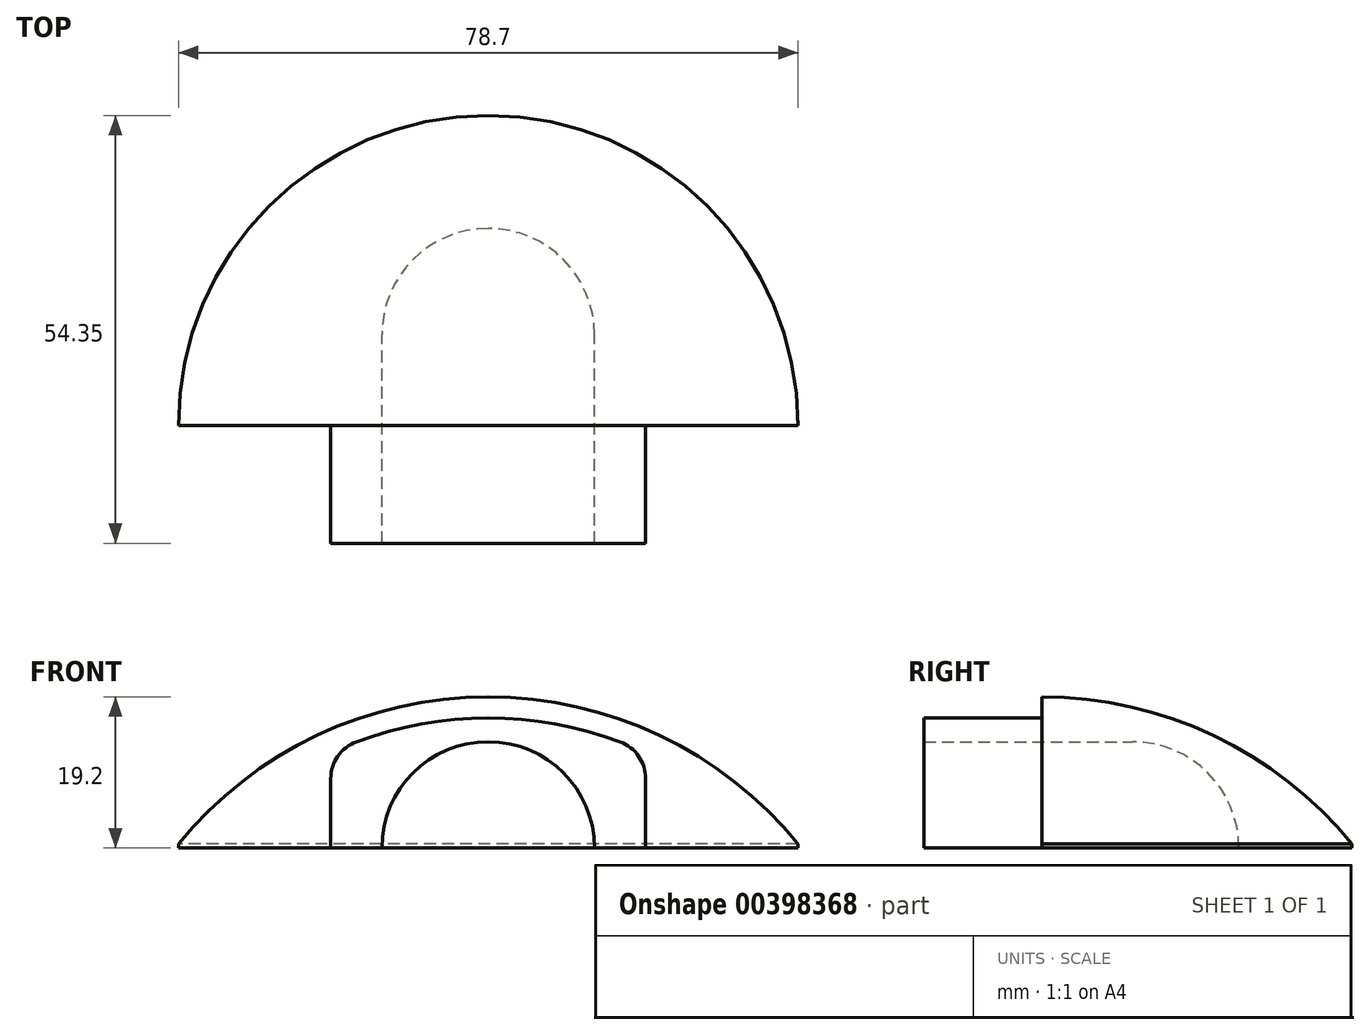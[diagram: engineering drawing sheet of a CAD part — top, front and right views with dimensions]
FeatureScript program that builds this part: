
annotation { "Feature Type Name" : "Feature", "Feature Type Description" : "" }
export const myFeature = defineFeature(function(context is Context, id is Id, definition is map)
    precondition{}
    {
        {
            var Q0;
            Q0=qCreatedBy(makeId("Front.planeOp"),FACE);
            var sketch = newSketch(context, id + "F0", { "sketchPlane" : qUnion([Q0])});
            skLineSegment(sketch, "E0", {"start": v(-39.5, 0) * mm, "end": v(39.5, 0) * mm});
            skPoint(sketch, "E1", {"position": v(0, 19) * mm});
            skLineSegment(sketch, "E2", {"start": v(39.5, 0) * mm, "end": v(39.5, 0) * mm});
            skLineSegment(sketch, "E3.MirrorCS", {"start": v(-39.5, 0) * mm, "end": v(-39.5, 0) * mm});
            skArc(sketch, "E4", {"start": v(39.5, 0) * mm, "mid": v(0, 19) * mm, "end": v(-39.5, 0) * mm});
            skSolve(sketch);
        }
        {
            var Q0;
            Q0=qCreatedBy(makeId("Front.planeOp"),FACE);
            var sketch = newSketch(context, id + "F1", { "sketchPlane" : qUnion([Q0])});
            skLineSegment(sketch, "E5.0", {"start": v(-39.35, 0) * mm, "end": v(0, 0) * mm});
            skArc(sketch, "E6.0", {"start": v(0, 19.2) * mm, "mid": v(-21.79, 14.29) * mm, "end": v(-39.35, 0.5) * mm});
            skLineSegment(sketch, "E7", {"start": v(0, 19.2) * mm, "end": v(0, 0) * mm});
            skLineSegment(sketch, "E8", {"start": v(-39.35, 0.5) * mm, "end": v(-39.35, 0) * mm});
            skSolve(sketch);
        }
        {
            var Q0;
            Q0 = qSketchRegion(id + "F1", true);
            var Q1;
            Q1=sQuery(id+"F1.wireOp",EDGE,"E7");
            revolve(context, id + "F2", {"entities" : qUnion([Q0]), "axis" : qUnion([Q1]), "revolveType" : RevolveType.ONE_DIRECTION, "angle" : 180 * degree});
        }
        {
            var Q0;
            Q0=qCreatedBy(makeId("Front.planeOp"),FACE);
            var sketch = newSketch(context, id + "F3", { "sketchPlane" : qUnion([Q0])});
            skArc(sketch, "E9.0", {"start": v(20, 12.14) * mm, "mid": v(0, 16.5) * mm, "end": v(-20, 12.14) * mm});
            skLineSegment(sketch, "E10", {"start": v(-20, 0) * mm, "end": v(20, 0) * mm});
            skLineSegment(sketch, "E11", {"start": v(20, 0) * mm, "end": v(20, 12.14) * mm});
            skLineSegment(sketch, "E12.MirrorCS", {"start": v(-20, 0) * mm, "end": v(-20, 12.14) * mm});
            skPoint(sketch, "E13.orphan", {"position": v(-36.25, 0) * mm});
            skSolve(sketch);
        }
        {
            var Q0;
            Q0 = qSketchRegion(id + "F3", true);
            extrude(context, id + "F4", {"entities" : qUnion([Q0]), "operationType" : NewBodyOperationType.ADD, "depth" : 15 * mm});
        }
        {
            var Q0;
            Q0=qCreatedBy(makeId("Top.planeOp"),FACE);
            var sketch = newSketch(context, id + "F5", { "sketchPlane" : qUnion([Q0])});
            skLineSegment(sketch, "E14.bottom", {"start": v(0, -15) * mm, "end": v(-13.5, -15) * mm});
            skLineSegment(sketch, "E14.left", {"start": v(0, -15) * mm, "end": v(0, 25) * mm});
            skLineSegment(sketch, "E14.right", {"start": v(-13.5, -15) * mm, "end": v(-13.5, 11.5) * mm});
            skArc(sketch, "E15", {"start": v(0, 25) * mm, "mid": v(-9.55, 21.05) * mm, "end": v(-13.5, 11.5) * mm});
            skSolve(sketch);
        }
        {
            var Q0;
            Q0=makeQuery(id+"F5.imprint","IMPRINT",FACE,{"disambiguationData":[TD([[makeQuery(id+"F5.imprint","IMPRINT",EDGE,{"derivedFrom":sQuery(id+"F5.wireOp",EDGE,"E14.bottom")}),-1.0]])]});
            var Q1;
            Q1=sQuery(id+"F5.wireOp",EDGE,"E14.left");
            revolve(context, id + "F6", {"operationType" : NewBodyOperationType.REMOVE, "entities" : qUnion([Q0]), "axis" : qUnion([Q1]), "revolveType" : RevolveType.FULL, "oppositeDirection" : true});
        }
        {
            var Q0;
            Q0=makeQuery(id+"F4.opExtrude","SWEPT_EDGE",EDGE,{"disambiguationData":[OSD([sQuery(id+"F3.wireOp",EDGE,"E9.0"),sQuery(id+"F3.wireOp",EDGE,"E12.MirrorCS")])]});
            var Q1;
            Q1=makeQuery(id+"F4.opExtrude","SWEPT_EDGE",EDGE,{"disambiguationData":[OSD([sQuery(id+"F3.wireOp",EDGE,"E9.0"),sQuery(id+"F3.wireOp",EDGE,"E11")])]});
            fillet(context, id + "F7", {"entities" : qUnion([Q0, Q1]), "radius" : 5 * mm, "tangentPropagation" : true, "allowEdgeOverflow" : false});
        }
    });
